# Revit family: Haworth_Pebble_Ottoman
name_source: partatom
category: Furniture
revit_build: Autodesk Revit 2018 (Build: 20170223_1515(x64)
units: mm (PartAtom-declared; Revit-internal decimal feet)

## family parameters
Always vertical = Yes
Cut with Voids When Loaded = No
OmniClass Number = 23.40.70.14.64.21
OmniClass Title = Systems Furniture
Room Calculation Point = No
Shared = No
Work Plane-Based = No

## types (4) — shared parameters
Actual Height = 17"
Assembly Code = E2020200
Custom Size = No
Custom Width = No
Description = Haworth Pebble Ottoman
Manufacturer = Haworth
Max. Depth = 47"
Max. Width = 67"
Min. Depth = 36"
Min. Width = 26"
Model = STSN
Revision Number = 1
Size = Verify Final Dim. w/ Haworth
Standard Depth x Width = 26x26 in., 34x34 in., 47x47 in., 34x67 in.
Standard Heights = 17 in.
URL = http://www.haworth.com
URL - Product = http://www.haworth.com
Warranty = http://www.haworth.com

## per-type parameters (varying)
| type | Actual Depth | Actual Width | Depth | Large | Medium | Mini | Small | Width |
| 34d 34w 17h | 36" | 34" | 34" | No | No | No | Yes | 34" |
| 47d 47w 17h | 47" | 47" | 47" | No | Yes | No | No | 47" |
| 34d 67w 17h | 36" | 67" | 34" | Yes | No | No | No | 67" |
| 26d 26w 17h | 36" | 26" | 26" | No | No | Yes | No | 26" |

## geometry (parser evidence)
native form markers: Sweep x3
no freeform markers — native parametric forms only
